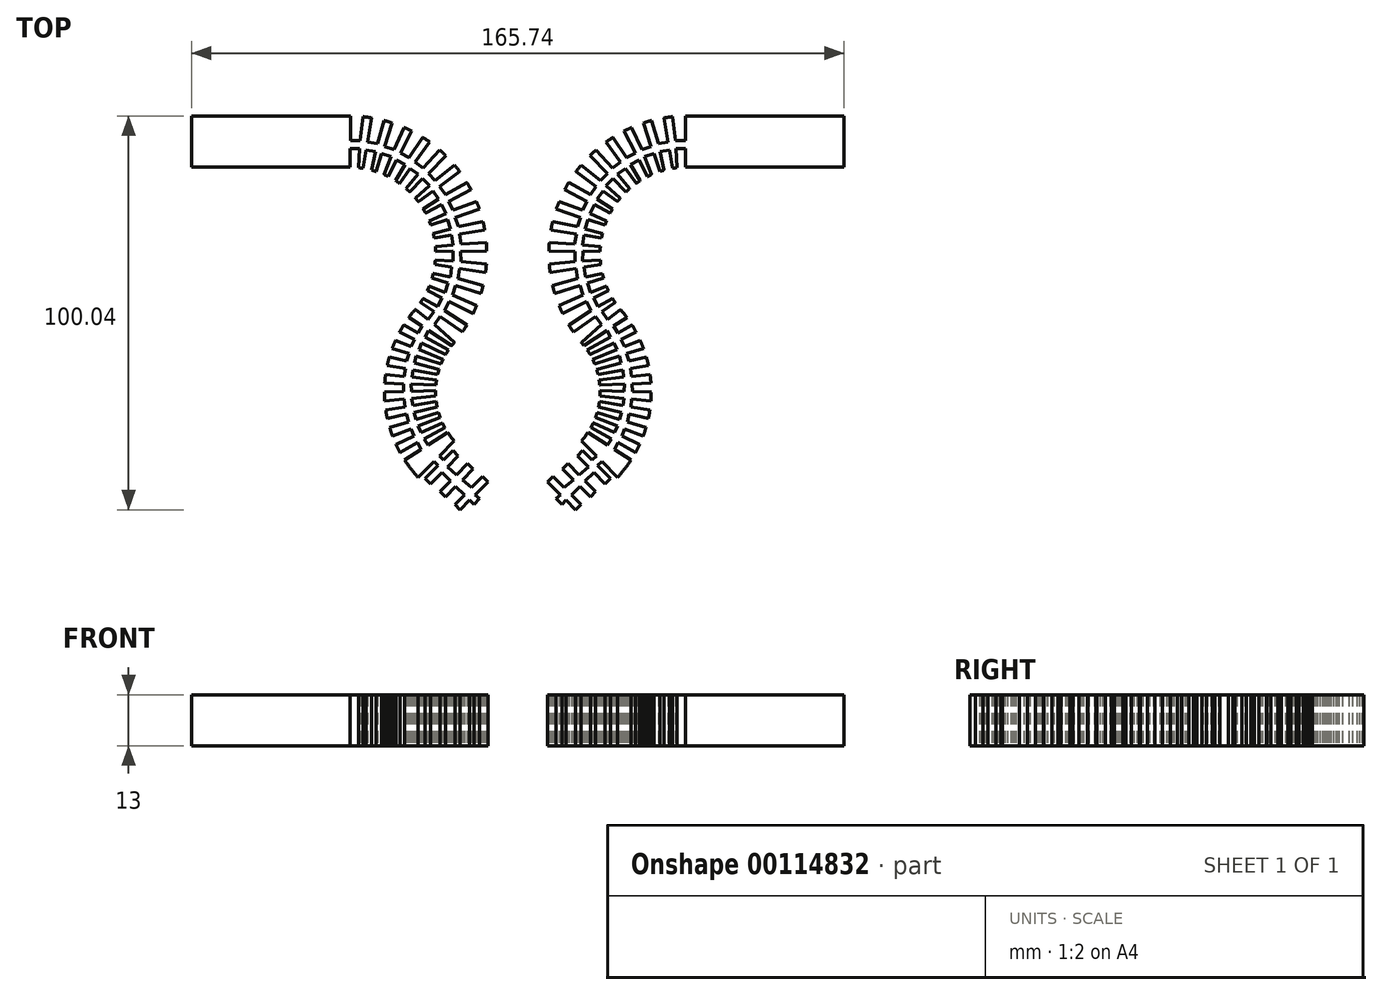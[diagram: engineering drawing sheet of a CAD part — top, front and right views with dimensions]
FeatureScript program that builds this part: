
annotation { "Feature Type Name" : "Feature", "Feature Type Description" : "" }
export const myFeature = defineFeature(function(context is Context, id is Id, definition is map)
    precondition{}
    {
        {
            var Q0;
            Q0=qCreatedBy(makeId("Top.planeOp"),FACE);
            var sketch = newSketch(context, id + "F0", { "sketchPlane" : qUnion([Q0])});
            skLineSegment(sketch, "E0", {"start": v(-77.87, 44.79) * mm, "end": v(-37.87, 44.79) * mm});
            skArc(sketch, "E1", {"start": v(-37.87, 44.79) * mm, "mid": v(-17.9, 31.98) * mm, "end": v(-21.2, 8.47) * mm});
            skArc(sketch, "E2", {"start": v(-21.2, 8.47) * mm, "mid": v(-28.89, -12.94) * mm, "end": v(-20.32, -34.02) * mm});
            skArc(sketch, "E3.0", {"start": v(-11.34, 0) * mm, "mid": v(-15.9, -12.42) * mm, "end": v(-11.16, -24.77) * mm});
            skArc(sketch, "E3.1", {"start": v(-37.87, 57.79) * mm, "mid": v(-6.08, 37.4) * mm, "end": v(-11.34, 0) * mm});
            skLineSegment(sketch, "E3.2", {"start": v(-77.87, 57.79) * mm, "end": v(-37.87, 57.79) * mm});
            skLineSegment(sketch, "E4", {"start": v(-77.87, 57.79) * mm, "end": v(-77.87, 44.79) * mm});
            skLineSegment(sketch, "E5", {"start": v(-77.87, 51.29) * mm, "end": v(-37.87, 51.29) * mm, "construction": true});
            skArc(sketch, "E6", {"start": v(-37.87, 51.29) * mm, "mid": v(-12.46, 35.34) * mm, "end": v(-15.76, 5.52) * mm, "construction": true});
            skArc(sketch, "E7", {"start": v(-15.76, 5.52) * mm, "mid": v(-21.7, -14) * mm, "end": v(-12.62, -32.27) * mm, "construction": true});
            skLineSegment(sketch, "E8", {"start": v(-4.75, -39.45) * mm, "end": v(-6.16, -40.87) * mm});
            skPoint(sketch, "E9.orphan", {"position": v(-7.33, -47) * mm});
            skPoint(sketch, "E10.orphan", {"position": v(-12.22, -47) * mm});
            skLineSegment(sketch, "E11", {"start": v(-12.62, -32.27) * mm, "end": v(-1.37, -43.41) * mm, "construction": true});
            skLineSegment(sketch, "E12", {"start": v(-2.6, -35.15) * mm, "end": v(-5.9, -38.47) * mm});
            skLineSegment(sketch, "E13", {"start": v(-9.64, -42.25) * mm, "end": v(-11, -40.92) * mm});
            skLineSegment(sketch, "E14", {"start": v(-11, -40.92) * mm, "end": v(-8.58, -38.48) * mm});
            skLineSegment(sketch, "E15", {"start": v(-2.6, -35.15) * mm, "end": v(-3.96, -33.8) * mm});
            skLineSegment(sketch, "E16", {"start": v(-14.32, -32.8) * mm, "end": v(-12.12, -34.96) * mm});
            skLineSegment(sketch, "E17.1.0.0", {"start": v(-6.37, -31.86) * mm, "end": v(-7.73, -30.52) * mm});
            skLineSegment(sketch, "E17.1.0.1", {"start": v(-6.37, -31.86) * mm, "end": v(-9.11, -34.63) * mm});
            skLineSegment(sketch, "E17.1.0.2", {"start": v(-13.4, -38.97) * mm, "end": v(-14.76, -37.63) * mm});
            skLineSegment(sketch, "E17.1.0.3", {"start": v(-14.76, -37.63) * mm, "end": v(-12.12, -34.96) * mm});
            skLineSegment(sketch, "E17.2.0.0", {"start": v(-10.14, -28.57) * mm, "end": v(-11.5, -27.23) * mm});
            skLineSegment(sketch, "E17.2.0.1", {"start": v(-10.14, -28.57) * mm, "end": v(-12.91, -31.37) * mm});
            skLineSegment(sketch, "E17.2.0.2", {"start": v(-17.18, -35.68) * mm, "end": v(-18.53, -34.34) * mm});
            skLineSegment(sketch, "E17.2.0.3", {"start": v(-18.53, -34.34) * mm, "end": v(-15.27, -31.05) * mm});
            skLineSegment(sketch, "E17.direction1", {"start": v(-3.96, -33.8) * mm, "end": v(-7.73, -30.52) * mm, "construction": true});
            skLineSegment(sketch, "E18", {"start": v(-11.16, -24.77) * mm, "end": v(-14.93, -28.58) * mm});
            skLineSegment(sketch, "E19", {"start": v(-14.93, -28.58) * mm, "end": v(-13.87, -29.63) * mm});
            skLineSegment(sketch, "E20", {"start": v(-20.32, -34.02) * mm, "end": v(-16.34, -30) * mm});
            skLineSegment(sketch, "E21", {"start": v(-16.34, -30) * mm, "end": v(-15.27, -31.05) * mm});
            skPoint(sketch, "E22.start.orphan", {"position": v(-8.39, -27.33) * mm});
            skPoint(sketch, "E23.orphan", {"position": v(0, -34.64) * mm});
            skPoint(sketch, "E24.orphan", {"position": v(-16.86, -37.21) * mm});
            skLineSegment(sketch, "E25.trimOffspring", {"start": v(-14.32, -32.8) * mm, "end": v(-17.18, -35.68) * mm});
            skLineSegment(sketch, "E26.trimOffspring", {"start": v(-10.56, -33.39) * mm, "end": v(-7.73, -30.52) * mm});
            skLineSegment(sketch, "E27.trimOffspring", {"start": v(-13.87, -29.63) * mm, "end": v(-11.5, -27.23) * mm});
            skLineSegment(sketch, "E28.trimOffspring", {"start": v(-10.77, -36.3) * mm, "end": v(-8.58, -38.48) * mm});
            skLineSegment(sketch, "E29.trimOffspring", {"start": v(-10.77, -36.3) * mm, "end": v(-13.4, -38.97) * mm});
            skLineSegment(sketch, "E30.trimOffspring", {"start": v(-6.76, -36.64) * mm, "end": v(-3.96, -33.8) * mm});
            skLineSegment(sketch, "E31.trimOffspring", {"start": v(-7.23, -39.81) * mm, "end": v(-9.64, -42.25) * mm});
            skLineSegment(sketch, "E32.trimOffspring", {"start": v(-6.76, -36.64) * mm, "end": v(-9.11, -34.63) * mm});
            skLineSegment(sketch, "E33.trimOffspring", {"start": v(-7.23, -39.81) * mm, "end": v(-6.16, -40.87) * mm});
            skLineSegment(sketch, "E34.trimOffspring", {"start": v(-10.56, -33.39) * mm, "end": v(-12.91, -31.37) * mm});
            skLineSegment(sketch, "E35", {"start": v(-5.9, -38.47) * mm, "end": v(-4.75, -39.45) * mm});
            skSolve(sketch);
        }
        {
            var Q0;
            Q0=makeQuery(id+"F0.imprint","IMPRINT",FACE,{"disambiguationData":[TD([[makeQuery(id+"F0.imprint","IMPRINT",EDGE,{"derivedFrom":sQuery(id+"F0.wireOp",EDGE,"E0")}),1.0]])]});
            extrude(context, id + "F1", {"entities" : qUnion([Q0]), "depth" : 13 * mm});
        }
        {
            var Q0;
            Q0=qCreatedBy(makeId("Top.planeOp"),FACE);
            var sketch = newSketch(context, id + "F2", { "sketchPlane" : qUnion([Q0])});
            skLineSegment(sketch, "E36", {"start": v(-66.67, 50.5) * mm, "end": v(-37.77, 50.5) * mm, "construction": true});
            skArc(sketch, "E37", {"start": v(-37.77, 50.5) * mm, "mid": v(-13.23, 35.1) * mm, "end": v(-16.42, 6.3) * mm, "construction": true});
            skArc(sketch, "E38", {"start": v(-16.42, 6.3) * mm, "mid": v(-22.5, -13.28) * mm, "end": v(-13.17, -31.54) * mm, "construction": true});
            skLineSegment(sketch, "E39.bottom", {"start": v(-37.54, 51.5) * mm, "end": v(-35.04, 51.5) * mm});
            skLineSegment(sketch, "E39.top", {"start": v(-37.54, 59.7) * mm, "end": v(-34.04, 59.7) * mm});
            skLineSegment(sketch, "E39.left", {"start": v(-37.54, 51.5) * mm, "end": v(-37.54, 59.7) * mm});
            skLineSegment(sketch, "E39.right", {"start": v(-35.04, 51.5) * mm, "end": v(-34.04, 59.7) * mm});
            skLineSegment(sketch, "E40.bottom", {"start": v(-37.65, 33.82) * mm, "end": v(-36.15, 33.82) * mm});
            skLineSegment(sketch, "E40.top", {"start": v(-37.65, 49.5) * mm, "end": v(-35.15, 49.5) * mm});
            skLineSegment(sketch, "E40.left", {"start": v(-37.65, 33.82) * mm, "end": v(-37.65, 49.5) * mm});
            skLineSegment(sketch, "E40.right", {"start": v(-36.15, 33.82) * mm, "end": v(-35.15, 49.5) * mm});
            skLineSegment(sketch, "E41.1.0", {"start": v(-30.68, 50.73) * mm, "end": v(-28.42, 58.69) * mm});
            skLineSegment(sketch, "E41.1.1", {"start": v(-33.15, 51.12) * mm, "end": v(-31.88, 59.23) * mm});
            skLineSegment(sketch, "E41.1.2", {"start": v(-34.53, 33.44) * mm, "end": v(-31.1, 48.77) * mm});
            skLineSegment(sketch, "E41.1.3", {"start": v(-36.01, 33.67) * mm, "end": v(-33.58, 49.16) * mm});
            skLineSegment(sketch, "E41.1.4", {"start": v(-31.88, 59.23) * mm, "end": v(-28.42, 58.69) * mm});
            skLineSegment(sketch, "E41.1.5", {"start": v(-33.15, 51.12) * mm, "end": v(-30.68, 50.73) * mm});
            skLineSegment(sketch, "E41.1.6", {"start": v(-33.58, 49.16) * mm, "end": v(-31.1, 48.77) * mm});
            skLineSegment(sketch, "E41.1.7", {"start": v(-36.01, 33.67) * mm, "end": v(-34.53, 33.44) * mm});
            skLineSegment(sketch, "E41.2.0", {"start": v(-26.5, 49.3) * mm, "end": v(-23.03, 56.8) * mm});
            skLineSegment(sketch, "E41.2.1", {"start": v(-28.88, 50.06) * mm, "end": v(-26.37, 57.88) * mm});
            skLineSegment(sketch, "E41.2.2", {"start": v(-32.99, 32.81) * mm, "end": v(-27.23, 47.43) * mm});
            skLineSegment(sketch, "E41.2.3", {"start": v(-34.41, 33.27) * mm, "end": v(-29.6, 48.2) * mm});
            skLineSegment(sketch, "E41.2.4", {"start": v(-26.37, 57.88) * mm, "end": v(-23.03, 56.8) * mm});
            skLineSegment(sketch, "E41.2.5", {"start": v(-28.88, 50.06) * mm, "end": v(-26.5, 49.3) * mm});
            skLineSegment(sketch, "E41.2.6", {"start": v(-29.6, 48.2) * mm, "end": v(-27.23, 47.43) * mm});
            skLineSegment(sketch, "E41.2.7", {"start": v(-34.41, 33.27) * mm, "end": v(-32.99, 32.81) * mm});
            skLineSegment(sketch, "E41.3.0", {"start": v(-22.6, 47.23) * mm, "end": v(-18, 54.11) * mm});
            skLineSegment(sketch, "E41.3.1", {"start": v(-24.83, 48.36) * mm, "end": v(-21.13, 55.69) * mm});
            skLineSegment(sketch, "E41.3.2", {"start": v(-31.56, 31.95) * mm, "end": v(-23.6, 45.5) * mm});
            skLineSegment(sketch, "E41.3.3", {"start": v(-32.9, 32.63) * mm, "end": v(-25.83, 46.63) * mm});
            skLineSegment(sketch, "E41.3.4", {"start": v(-21.13, 55.69) * mm, "end": v(-18, 54.11) * mm});
            skLineSegment(sketch, "E41.3.5", {"start": v(-24.83, 48.36) * mm, "end": v(-22.6, 47.23) * mm});
            skLineSegment(sketch, "E41.3.6", {"start": v(-25.83, 46.63) * mm, "end": v(-23.6, 45.5) * mm});
            skLineSegment(sketch, "E41.3.7", {"start": v(-32.9, 32.63) * mm, "end": v(-31.56, 31.95) * mm});
            skLineSegment(sketch, "E41.4.0", {"start": v(-19.06, 44.59) * mm, "end": v(-13.45, 50.67) * mm});
            skLineSegment(sketch, "E41.4.1", {"start": v(-21.09, 46.05) * mm, "end": v(-16.3, 52.71) * mm});
            skLineSegment(sketch, "E41.4.2", {"start": v(-30.28, 30.88) * mm, "end": v(-20.32, 43.03) * mm});
            skLineSegment(sketch, "E41.4.3", {"start": v(-31.5, 31.76) * mm, "end": v(-22.35, 44.5) * mm});
            skLineSegment(sketch, "E41.4.4", {"start": v(-16.3, 52.71) * mm, "end": v(-13.45, 50.67) * mm});
            skLineSegment(sketch, "E41.4.5", {"start": v(-21.09, 46.05) * mm, "end": v(-19.06, 44.59) * mm});
            skLineSegment(sketch, "E41.4.6", {"start": v(-22.35, 44.5) * mm, "end": v(-20.32, 43.03) * mm});
            skLineSegment(sketch, "E41.4.7", {"start": v(-31.5, 31.76) * mm, "end": v(-30.28, 30.88) * mm});
            skLineSegment(sketch, "E41.5.0", {"start": v(-15.97, 41.42) * mm, "end": v(-9.5, 46.56) * mm});
            skLineSegment(sketch, "E41.5.1", {"start": v(-17.75, 43.18) * mm, "end": v(-11.98, 49.02) * mm});
            skLineSegment(sketch, "E41.5.2", {"start": v(-29.19, 29.63) * mm, "end": v(-17.46, 40.08) * mm});
            skLineSegment(sketch, "E41.5.3", {"start": v(-30.26, 30.68) * mm, "end": v(-19.24, 41.84) * mm});
            skLineSegment(sketch, "E41.5.4", {"start": v(-11.98, 49.02) * mm, "end": v(-9.5, 46.56) * mm});
            skLineSegment(sketch, "E41.5.5", {"start": v(-17.75, 43.18) * mm, "end": v(-15.97, 41.42) * mm});
            skLineSegment(sketch, "E41.5.6", {"start": v(-19.24, 41.84) * mm, "end": v(-17.46, 40.08) * mm});
            skLineSegment(sketch, "E41.5.7", {"start": v(-30.26, 30.68) * mm, "end": v(-29.19, 29.63) * mm});
            skLineSegment(sketch, "E41.6.0", {"start": v(-13.41, 37.82) * mm, "end": v(-6.21, 41.9) * mm});
            skLineSegment(sketch, "E41.6.1", {"start": v(-14.9, 39.83) * mm, "end": v(-8.3, 44.7) * mm});
            skLineSegment(sketch, "E41.6.2", {"start": v(-28.3, 28.22) * mm, "end": v(-15.1, 36.73) * mm});
            skLineSegment(sketch, "E41.6.3", {"start": v(-29.2, 29.43) * mm, "end": v(-16.58, 38.74) * mm});
            skLineSegment(sketch, "E41.6.4", {"start": v(-8.3, 44.7) * mm, "end": v(-6.21, 41.9) * mm});
            skLineSegment(sketch, "E41.6.5", {"start": v(-14.9, 39.83) * mm, "end": v(-13.41, 37.82) * mm});
            skLineSegment(sketch, "E41.6.6", {"start": v(-16.58, 38.74) * mm, "end": v(-15.1, 36.73) * mm});
            skLineSegment(sketch, "E41.6.7", {"start": v(-29.2, 29.43) * mm, "end": v(-28.3, 28.22) * mm});
            skLineSegment(sketch, "E41.7.0", {"start": v(-11.45, 33.86) * mm, "end": v(-3.7, 36.77) * mm});
            skLineSegment(sketch, "E41.7.1", {"start": v(-12.6, 36.08) * mm, "end": v(-5.32, 39.87) * mm});
            skLineSegment(sketch, "E41.7.2", {"start": v(-27.64, 26.69) * mm, "end": v(-13.27, 33.04) * mm});
            skLineSegment(sketch, "E41.7.3", {"start": v(-28.34, 28.02) * mm, "end": v(-14.43, 35.26) * mm});
            skLineSegment(sketch, "E41.7.4", {"start": v(-5.32, 39.87) * mm, "end": v(-3.7, 36.77) * mm});
            skLineSegment(sketch, "E41.7.5", {"start": v(-12.6, 36.08) * mm, "end": v(-11.45, 33.86) * mm});
            skLineSegment(sketch, "E41.7.6", {"start": v(-14.43, 35.26) * mm, "end": v(-13.27, 33.04) * mm});
            skLineSegment(sketch, "E41.7.7", {"start": v(-28.34, 28.02) * mm, "end": v(-27.64, 26.69) * mm});
            skLineSegment(sketch, "E41.8.0", {"start": v(-10.12, 29.65) * mm, "end": v(-2.02, 31.32) * mm});
            skLineSegment(sketch, "E41.8.1", {"start": v(-10.91, 32.02) * mm, "end": v(-3.13, 34.63) * mm});
            skLineSegment(sketch, "E41.8.2", {"start": v(-27.23, 25.08) * mm, "end": v(-12.05, 29.12) * mm});
            skLineSegment(sketch, "E41.8.3", {"start": v(-27.7, 26.5) * mm, "end": v(-12.84, 31.5) * mm});
            skLineSegment(sketch, "E41.8.4", {"start": v(-3.13, 34.63) * mm, "end": v(-2.02, 31.32) * mm});
            skLineSegment(sketch, "E41.8.5", {"start": v(-10.91, 32.02) * mm, "end": v(-10.12, 29.65) * mm});
            skLineSegment(sketch, "E41.8.6", {"start": v(-12.84, 31.5) * mm, "end": v(-12.05, 29.12) * mm});
            skLineSegment(sketch, "E41.8.7", {"start": v(-27.7, 26.5) * mm, "end": v(-27.23, 25.08) * mm});
            skLineSegment(sketch, "E41.9.0", {"start": v(-9.46, 25.28) * mm, "end": v(-1.2, 25.67) * mm});
            skLineSegment(sketch, "E41.9.1", {"start": v(-9.88, 27.74) * mm, "end": v(-1.78, 29.12) * mm});
            skLineSegment(sketch, "E41.9.2", {"start": v(-27.07, 23.42) * mm, "end": v(-11.45, 25.06) * mm});
            skLineSegment(sketch, "E41.9.3", {"start": v(-27.33, 24.9) * mm, "end": v(-11.87, 27.52) * mm});
            skLineSegment(sketch, "E41.9.4", {"start": v(-1.78, 29.12) * mm, "end": v(-1.2, 25.67) * mm});
            skLineSegment(sketch, "E41.9.5", {"start": v(-9.88, 27.74) * mm, "end": v(-9.46, 25.28) * mm});
            skLineSegment(sketch, "E41.9.6", {"start": v(-11.87, 27.52) * mm, "end": v(-11.45, 25.06) * mm});
            skLineSegment(sketch, "E41.9.7", {"start": v(-27.33, 24.9) * mm, "end": v(-27.07, 23.42) * mm});
            skLineSegment(sketch, "E41.10.0", {"start": v(-9.48, 20.86) * mm, "end": v(-1.26, 19.96) * mm});
            skLineSegment(sketch, "E41.10.1", {"start": v(-9.51, 23.36) * mm, "end": v(-1.3, 23.46) * mm});
            skLineSegment(sketch, "E41.10.2", {"start": v(-27.18, 21.75) * mm, "end": v(-11.48, 20.95) * mm});
            skLineSegment(sketch, "E41.10.3", {"start": v(-27.2, 23.25) * mm, "end": v(-11.52, 23.45) * mm});
            skLineSegment(sketch, "E41.10.4", {"start": v(-1.3, 23.46) * mm, "end": v(-1.26, 19.96) * mm});
            skLineSegment(sketch, "E41.10.5", {"start": v(-9.51, 23.36) * mm, "end": v(-9.48, 20.86) * mm});
            skLineSegment(sketch, "E41.10.6", {"start": v(-11.52, 23.45) * mm, "end": v(-11.48, 20.95) * mm});
            skLineSegment(sketch, "E41.10.7", {"start": v(-27.2, 23.25) * mm, "end": v(-27.18, 21.75) * mm});
            skLineSegment(sketch, "E41.11.0", {"start": v(-10.2, 16.5) * mm, "end": v(-2.21, 14.34) * mm});
            skLineSegment(sketch, "E41.11.1", {"start": v(-9.84, 18.97) * mm, "end": v(-1.71, 17.8) * mm});
            skLineSegment(sketch, "E41.11.2", {"start": v(-27.54, 20.13) * mm, "end": v(-12.16, 16.9) * mm});
            skLineSegment(sketch, "E41.11.3", {"start": v(-27.32, 21.61) * mm, "end": v(-11.8, 19.37) * mm});
            skLineSegment(sketch, "E41.11.4", {"start": v(-1.71, 17.8) * mm, "end": v(-2.21, 14.34) * mm});
            skLineSegment(sketch, "E41.11.5", {"start": v(-9.84, 18.97) * mm, "end": v(-10.2, 16.5) * mm});
            skLineSegment(sketch, "E41.11.6", {"start": v(-11.8, 19.37) * mm, "end": v(-12.16, 16.9) * mm});
            skLineSegment(sketch, "E41.11.7", {"start": v(-27.32, 21.61) * mm, "end": v(-27.54, 20.13) * mm});
            skLineSegment(sketch, "E41.12.0", {"start": v(-11.58, 12.3) * mm, "end": v(-4.03, 8.93) * mm});
            skLineSegment(sketch, "E41.12.1", {"start": v(-10.84, 14.69) * mm, "end": v(-3, 12.27) * mm});
            skLineSegment(sketch, "E41.12.2", {"start": v(-28.14, 18.58) * mm, "end": v(-13.45, 13) * mm});
            skLineSegment(sketch, "E41.12.3", {"start": v(-27.7, 20.01) * mm, "end": v(-12.72, 15.39) * mm});
            skLineSegment(sketch, "E41.12.4", {"start": v(-3, 12.27) * mm, "end": v(-4.03, 8.93) * mm});
            skLineSegment(sketch, "E41.12.5", {"start": v(-10.84, 14.69) * mm, "end": v(-11.58, 12.3) * mm});
            skLineSegment(sketch, "E41.12.6", {"start": v(-12.72, 15.39) * mm, "end": v(-13.45, 13) * mm});
            skLineSegment(sketch, "E41.12.7", {"start": v(-27.7, 20.01) * mm, "end": v(-28.14, 18.58) * mm});
            skLineSegment(sketch, "E41.13.0", {"start": v(-13.6, 8.37) * mm, "end": v(-6.66, 3.86) * mm});
            skLineSegment(sketch, "E41.13.1", {"start": v(-12.5, 10.61) * mm, "end": v(-5.12, 7) * mm});
            skLineSegment(sketch, "E41.13.2", {"start": v(-28.98, 17.14) * mm, "end": v(-15.34, 9.35) * mm});
            skLineSegment(sketch, "E41.13.3", {"start": v(-28.32, 18.49) * mm, "end": v(-14.24, 11.6) * mm});
            skLineSegment(sketch, "E41.13.4", {"start": v(-5.12, 7) * mm, "end": v(-6.66, 3.86) * mm});
            skLineSegment(sketch, "E41.13.5", {"start": v(-12.5, 10.61) * mm, "end": v(-13.6, 8.37) * mm});
            skLineSegment(sketch, "E41.13.6", {"start": v(-14.24, 11.6) * mm, "end": v(-15.34, 9.35) * mm});
            skLineSegment(sketch, "E41.13.7", {"start": v(-28.32, 18.49) * mm, "end": v(-28.98, 17.14) * mm});
            skLineSegment(sketch, "E41.14.0", {"start": v(-16.2, 4.8) * mm, "end": v(-10.04, -0.73) * mm});
            skLineSegment(sketch, "E41.14.1", {"start": v(-14.76, 6.84) * mm, "end": v(-8.03, 2.13) * mm});
            skLineSegment(sketch, "E41.14.2", {"start": v(-30.04, 15.85) * mm, "end": v(-17.77, 6.04) * mm});
            skLineSegment(sketch, "E41.14.3", {"start": v(-29.18, 17.08) * mm, "end": v(-16.33, 8.08) * mm});
            skLineSegment(sketch, "E41.14.4", {"start": v(-8.03, 2.13) * mm, "end": v(-10.04, -0.73) * mm});
            skLineSegment(sketch, "E41.14.5", {"start": v(-14.76, 6.84) * mm, "end": v(-16.2, 4.8) * mm});
            skLineSegment(sketch, "E41.14.6", {"start": v(-16.33, 8.08) * mm, "end": v(-17.77, 6.04) * mm});
            skLineSegment(sketch, "E41.14.7", {"start": v(-29.18, 17.08) * mm, "end": v(-30.04, 15.85) * mm});
            skLineSegment(sketch, "E41.anchor1", {"start": v(-37.77, 23.24) * mm, "end": v(-37.65, 33.82) * mm, "construction": true});
            skLineSegment(sketch, "E41.anchor2", {"start": v(-37.77, 23.24) * mm, "end": v(-29.18, 17.08) * mm, "construction": true});
            skSolve(sketch);
        }
        {
            var Q0;
            Q0 = qSketchRegion(id + "F2", true);
            extrude(context, id + "F3", {"entities" : qUnion([Q0]), "operationType" : NewBodyOperationType.REMOVE, "endBound" : BoundingType.THROUGH_ALL, "depth" : 25 * mm});
        }
        {
            var Q0;
            Q0=qCreatedBy(makeId("Top.planeOp"),FACE);
            var sketch = newSketch(context, id + "F4", { "sketchPlane" : qUnion([Q0])});
            skLineSegment(sketch, "E42", {"start": v(-67.85, 51.08) * mm, "end": v(-38.46, 51.08) * mm, "construction": true});
            skArc(sketch, "E43", {"start": v(-38.46, 51.08) * mm, "mid": v(-13.5, 35.42) * mm, "end": v(-16.74, 6.13) * mm, "construction": true});
            skArc(sketch, "E44", {"start": v(-16.74, 6.13) * mm, "mid": v(-22.93, -13.8) * mm, "end": v(-13.43, -32.37) * mm, "construction": true});
            skLineSegment(sketch, "E45", {"start": v(4.62, -11.43) * mm, "end": v(-17.67, 3.3) * mm});
            skLineSegment(sketch, "E46", {"start": v(-26.5, 9.14) * mm, "end": v(-27.76, 6.87) * mm});
            skLineSegment(sketch, "E47", {"start": v(-27.76, 6.87) * mm, "end": v(-20.38, 2.7) * mm});
            skLineSegment(sketch, "E48", {"start": v(-17.67, 3.3) * mm, "end": v(-18.58, 1.68) * mm});
            skLineSegment(sketch, "E49", {"start": v(-20.38, 2.7) * mm, "end": v(-19.28, 4.37) * mm});
            skLineSegment(sketch, "E50.trimOffspring", {"start": v(-19.28, 4.37) * mm, "end": v(-26.5, 9.14) * mm});
            skLineSegment(sketch, "E51.trimOffspring", {"start": v(-18.58, 1.68) * mm, "end": v(4.62, -11.43) * mm});
            skLineSegment(sketch, "E52.1.0", {"start": v(4.62, -11.43) * mm, "end": v(-19.45, 0.15) * mm});
            skLineSegment(sketch, "E52.1.1", {"start": v(-28.99, 4.74) * mm, "end": v(-29.94, 2.32) * mm});
            skLineSegment(sketch, "E52.1.2", {"start": v(-20.14, -1.58) * mm, "end": v(4.62, -11.43) * mm});
            skLineSegment(sketch, "E52.1.3", {"start": v(-29.94, 2.32) * mm, "end": v(-22.07, -0.81) * mm});
            skLineSegment(sketch, "E52.1.4", {"start": v(-19.45, 0.15) * mm, "end": v(-20.14, -1.58) * mm});
            skLineSegment(sketch, "E52.1.5", {"start": v(-21.2, 1) * mm, "end": v(-28.99, 4.74) * mm});
            skLineSegment(sketch, "E52.1.6", {"start": v(-22.07, -0.81) * mm, "end": v(-21.2, 1) * mm});
            skLineSegment(sketch, "E52.2.0", {"start": v(4.62, -11.43) * mm, "end": v(-20.8, -3.21) * mm});
            skLineSegment(sketch, "E52.2.1", {"start": v(-30.87, 0.04) * mm, "end": v(-31.48, -2.48) * mm});
            skLineSegment(sketch, "E52.2.2", {"start": v(-21.25, -5.02) * mm, "end": v(4.62, -11.43) * mm});
            skLineSegment(sketch, "E52.2.3", {"start": v(-31.48, -2.48) * mm, "end": v(-23.26, -4.52) * mm});
            skLineSegment(sketch, "E52.2.4", {"start": v(-20.8, -3.21) * mm, "end": v(-21.25, -5.02) * mm});
            skLineSegment(sketch, "E52.2.5", {"start": v(-22.64, -2.62) * mm, "end": v(-30.87, 0.04) * mm});
            skLineSegment(sketch, "E52.2.6", {"start": v(-23.26, -4.52) * mm, "end": v(-22.64, -2.62) * mm});
            skLineSegment(sketch, "E52.3.0", {"start": v(4.62, -11.43) * mm, "end": v(-21.68, -6.73) * mm});
            skLineSegment(sketch, "E52.3.1", {"start": v(-32.1, -4.86) * mm, "end": v(-32.36, -7.45) * mm});
            skLineSegment(sketch, "E52.3.2", {"start": v(-21.88, -8.58) * mm, "end": v(4.62, -11.43) * mm});
            skLineSegment(sketch, "E52.3.3", {"start": v(-32.36, -7.45) * mm, "end": v(-23.93, -8.36) * mm});
            skLineSegment(sketch, "E52.3.4", {"start": v(-21.68, -6.73) * mm, "end": v(-21.88, -8.58) * mm});
            skLineSegment(sketch, "E52.3.5", {"start": v(-23.58, -6.39) * mm, "end": v(-32.1, -4.86) * mm});
            skLineSegment(sketch, "E52.3.6", {"start": v(-23.93, -8.36) * mm, "end": v(-23.58, -6.39) * mm});
            skLineSegment(sketch, "E52.4.0", {"start": v(4.62, -11.43) * mm, "end": v(-22.07, -10.33) * mm});
            skLineSegment(sketch, "E52.4.1", {"start": v(-32.64, -9.9) * mm, "end": v(-32.56, -12.5) * mm});
            skLineSegment(sketch, "E52.4.2", {"start": v(-22.02, -12.19) * mm, "end": v(4.62, -11.43) * mm});
            skLineSegment(sketch, "E52.4.3", {"start": v(-32.56, -12.5) * mm, "end": v(-24.09, -12.25) * mm});
            skLineSegment(sketch, "E52.4.4", {"start": v(-22.07, -10.33) * mm, "end": v(-22.02, -12.19) * mm});
            skLineSegment(sketch, "E52.4.5", {"start": v(-24, -10.25) * mm, "end": v(-32.64, -9.9) * mm});
            skLineSegment(sketch, "E52.4.6", {"start": v(-24.09, -12.25) * mm, "end": v(-24, -10.25) * mm});
            skLineSegment(sketch, "E52.5.0", {"start": v(4.62, -11.43) * mm, "end": v(-21.98, -13.95) * mm});
            skLineSegment(sketch, "E52.5.1", {"start": v(-32.5, -14.95) * mm, "end": v(-32.07, -17.51) * mm});
            skLineSegment(sketch, "E52.5.2", {"start": v(-21.67, -15.79) * mm, "end": v(4.62, -11.43) * mm});
            skLineSegment(sketch, "E52.5.3", {"start": v(-32.07, -17.51) * mm, "end": v(-23.71, -16.13) * mm});
            skLineSegment(sketch, "E52.5.4", {"start": v(-21.98, -13.95) * mm, "end": v(-21.67, -15.79) * mm});
            skLineSegment(sketch, "E52.5.5", {"start": v(-23.9, -14.13) * mm, "end": v(-32.5, -14.95) * mm});
            skLineSegment(sketch, "E52.5.6", {"start": v(-23.71, -16.13) * mm, "end": v(-23.9, -14.13) * mm});
            skLineSegment(sketch, "E52.6.0", {"start": v(4.62, -11.43) * mm, "end": v(-21.39, -17.53) * mm});
            skLineSegment(sketch, "E52.6.1", {"start": v(-31.69, -19.94) * mm, "end": v(-30.91, -22.42) * mm});
            skLineSegment(sketch, "E52.6.2", {"start": v(-20.84, -19.3) * mm, "end": v(4.62, -11.43) * mm});
            skLineSegment(sketch, "E52.6.3", {"start": v(-30.91, -22.42) * mm, "end": v(-22.82, -19.92) * mm});
            skLineSegment(sketch, "E52.6.4", {"start": v(-21.39, -17.53) * mm, "end": v(-20.84, -19.3) * mm});
            skLineSegment(sketch, "E52.6.5", {"start": v(-23.27, -17.97) * mm, "end": v(-31.69, -19.94) * mm});
            skLineSegment(sketch, "E52.6.6", {"start": v(-22.82, -19.92) * mm, "end": v(-23.27, -17.97) * mm});
            skLineSegment(sketch, "E52.7.0", {"start": v(4.62, -11.43) * mm, "end": v(-20.32, -20.99) * mm});
            skLineSegment(sketch, "E52.7.1", {"start": v(-30.2, -24.78) * mm, "end": v(-29.1, -27.13) * mm});
            skLineSegment(sketch, "E52.7.2", {"start": v(-19.54, -22.68) * mm, "end": v(4.62, -11.43) * mm});
            skLineSegment(sketch, "E52.7.3", {"start": v(-29.1, -27.13) * mm, "end": v(-21.41, -23.55) * mm});
            skLineSegment(sketch, "E52.7.4", {"start": v(-20.32, -20.99) * mm, "end": v(-19.54, -22.68) * mm});
            skLineSegment(sketch, "E52.7.5", {"start": v(-22.13, -21.68) * mm, "end": v(-30.2, -24.78) * mm});
            skLineSegment(sketch, "E52.7.6", {"start": v(-21.41, -23.55) * mm, "end": v(-22.13, -21.68) * mm});
            skLineSegment(sketch, "E52.8.0", {"start": v(4.62, -11.43) * mm, "end": v(-18.8, -24.28) * mm});
            skLineSegment(sketch, "E52.8.1", {"start": v(-28.08, -29.37) * mm, "end": v(-26.66, -31.55) * mm});
            skLineSegment(sketch, "E52.8.2", {"start": v(-17.8, -25.84) * mm, "end": v(4.62, -11.43) * mm});
            skLineSegment(sketch, "E52.8.3", {"start": v(-26.66, -31.55) * mm, "end": v(-19.53, -26.96) * mm});
            skLineSegment(sketch, "E52.8.4", {"start": v(-18.8, -24.28) * mm, "end": v(-17.8, -25.84) * mm});
            skLineSegment(sketch, "E52.8.5", {"start": v(-20.5, -25.2) * mm, "end": v(-28.08, -29.37) * mm});
            skLineSegment(sketch, "E52.8.6", {"start": v(-19.53, -26.96) * mm, "end": v(-20.5, -25.2) * mm});
            skLineSegment(sketch, "E52.anchor1", {"start": v(4.62, -11.43) * mm, "end": v(-27.76, 6.87) * mm, "construction": true});
            skSolve(sketch);
        }
        {
            var Q0;
            Q0 = qSketchRegion(id + "F4", true);
            extrude(context, id + "F5", {"entities" : qUnion([Q0]), "operationType" : NewBodyOperationType.REMOVE, "depth" : 25 * mm});
        }
        {
            var Q0;
            Q0=qCreatedBy(makeId("Right.planeOp"),FACE);
            cPlane(context, id + "F6", {"entities" : qUnion([Q0]), "cplaneType" : CPlaneType.OFFSET, "offset" : 5 * mm, "width" : 150 * mm, "height" : 150 * mm});
        }
        {
            var Q0;
            Q0=makeQuery(id+"F1.opExtrude","SWEPT_BODY",BODY,{"disambiguationData":[OSD([sQuery(id+"F0.wireOp",EDGE,"E0"),sQuery(id+"F0.wireOp",EDGE,"E1"),sQuery(id+"F0.wireOp",EDGE,"E2"),sQuery(id+"F0.wireOp",EDGE,"E3.0"),sQuery(id+"F0.wireOp",EDGE,"E3.1"),sQuery(id+"F0.wireOp",EDGE,"E3.2"),sQuery(id+"F0.wireOp",EDGE,"E4"),sQuery(id+"F0.wireOp",EDGE,"E8"),sQuery(id+"F0.wireOp",EDGE,"E12"),sQuery(id+"F0.wireOp",EDGE,"E13"),sQuery(id+"F0.wireOp",EDGE,"E14"),sQuery(id+"F0.wireOp",EDGE,"E15"),sQuery(id+"F0.wireOp",EDGE,"E16"),sQuery(id+"F0.wireOp",EDGE,"E17.1.0.0"),sQuery(id+"F0.wireOp",EDGE,"E17.1.0.1"),sQuery(id+"F0.wireOp",EDGE,"E17.1.0.2"),sQuery(id+"F0.wireOp",EDGE,"E17.1.0.3"),sQuery(id+"F0.wireOp",EDGE,"E17.2.0.0"),sQuery(id+"F0.wireOp",EDGE,"E17.2.0.1"),sQuery(id+"F0.wireOp",EDGE,"E17.2.0.2"),sQuery(id+"F0.wireOp",EDGE,"E18"),sQuery(id+"F0.wireOp",EDGE,"E19"),sQuery(id+"F0.wireOp",EDGE,"E20"),sQuery(id+"F0.wireOp",EDGE,"E21"),sQuery(id+"F0.wireOp",EDGE,"E25.trimOffspring"),sQuery(id+"F0.wireOp",EDGE,"E26.trimOffspring"),sQuery(id+"F0.wireOp",EDGE,"E27.trimOffspring"),sQuery(id+"F0.wireOp",EDGE,"E17.2.0.3"),sQuery(id+"F0.wireOp",EDGE,"E28.trimOffspring"),sQuery(id+"F0.wireOp",EDGE,"E29.trimOffspring"),sQuery(id+"F0.wireOp",EDGE,"E30.trimOffspring"),sQuery(id+"F0.wireOp",EDGE,"E31.trimOffspring"),sQuery(id+"F0.wireOp",EDGE,"E32.trimOffspring"),sQuery(id+"F0.wireOp",EDGE,"E33.trimOffspring"),sQuery(id+"F0.wireOp",EDGE,"E34.trimOffspring"),sQuery(id+"F0.wireOp",EDGE,"E35")])]});
            var Q1;
            Q1=qCreatedBy(id+"F6.planeOp",FACE);
            mirror(context, id + "F7", {"entities" : qUnion([Q0]), "mirrorPlane" : qUnion([Q1])});
        }
    });
